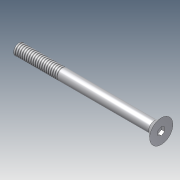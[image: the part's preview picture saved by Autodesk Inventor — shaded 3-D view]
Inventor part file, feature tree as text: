
AUTODESK INVENTOR PART (.ipt)
format: ipt  version: 2012 (Build 160160000, 160)  size: 91,648 bytes
history: native  units: in
note: dims shown in document units (in); Inventor stores cm internally (conversion verified against a paired STEP export)
features: sketch x2, revolve x1, thread x1, extrude x1
ambient origin geometry x8: Origin, YZ Plane, XZ Plane, XY Plane, X Axis, Y Axis, Z Axis, Center Point
bodies: Solid1 (feature_tree)
feature tree (5):
  revolve  "Revolution1"  [1 undecoded]
  thread  "Thread1"  [1 undecoded]
  sketch  "Sketch2"  dims[d4=90.0deg d5=1.0in d6=0.0in d16=0.1562in d17=0.075in d18=0.0in d19=3.25in]
  extrude  "Extrusion1"  Depth=1.0in TaperAngle=0.0deg
  sketch  "Sketch1"  dims[d0=0.125in d2=0.161in d3=0.2655in]
note: 2 required parameter values undecoded (feature->parameter linkage not recoverable at this tier; creation-order binding heuristic only, values carry confidence <= 0.55)